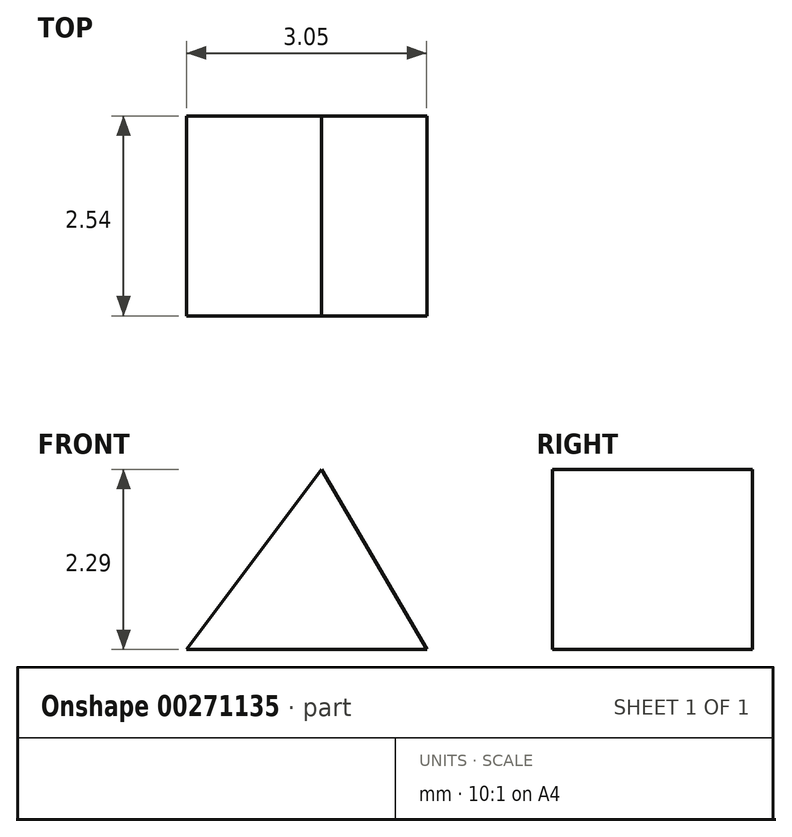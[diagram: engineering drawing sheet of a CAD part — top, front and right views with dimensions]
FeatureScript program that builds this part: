
annotation { "Feature Type Name" : "Feature", "Feature Type Description" : "" }
export const myFeature = defineFeature(function(context is Context, id is Id, definition is map)
    precondition{}
    {
        {
            var Q0;
            Q0=qCreatedBy(makeId("Front.planeOp"),FACE);
            var sketch = newSketch(context, id + "F0", { "sketchPlane" : qUnion([Q0])});
            skLineSegment(sketch, "E0", {"start": v(-52.32, 0) * mm, "end": v(-50.6, 2.3) * mm});
            skLineSegment(sketch, "E1", {"start": v(-50.6, 2.3) * mm, "end": v(-49.27, 0) * mm});
            skLineSegment(sketch, "E2", {"start": v(-49.27, 0) * mm, "end": v(-52.32, 0) * mm});
            skSolve(sketch);
        }
        {
            var Q0;
            Q0 = qSketchRegion(id + "F0", true);
            extrude(context, id + "F1", {"entities" : qUnion([Q0]), "depth" : 2.54 * mm});
        }
    });
